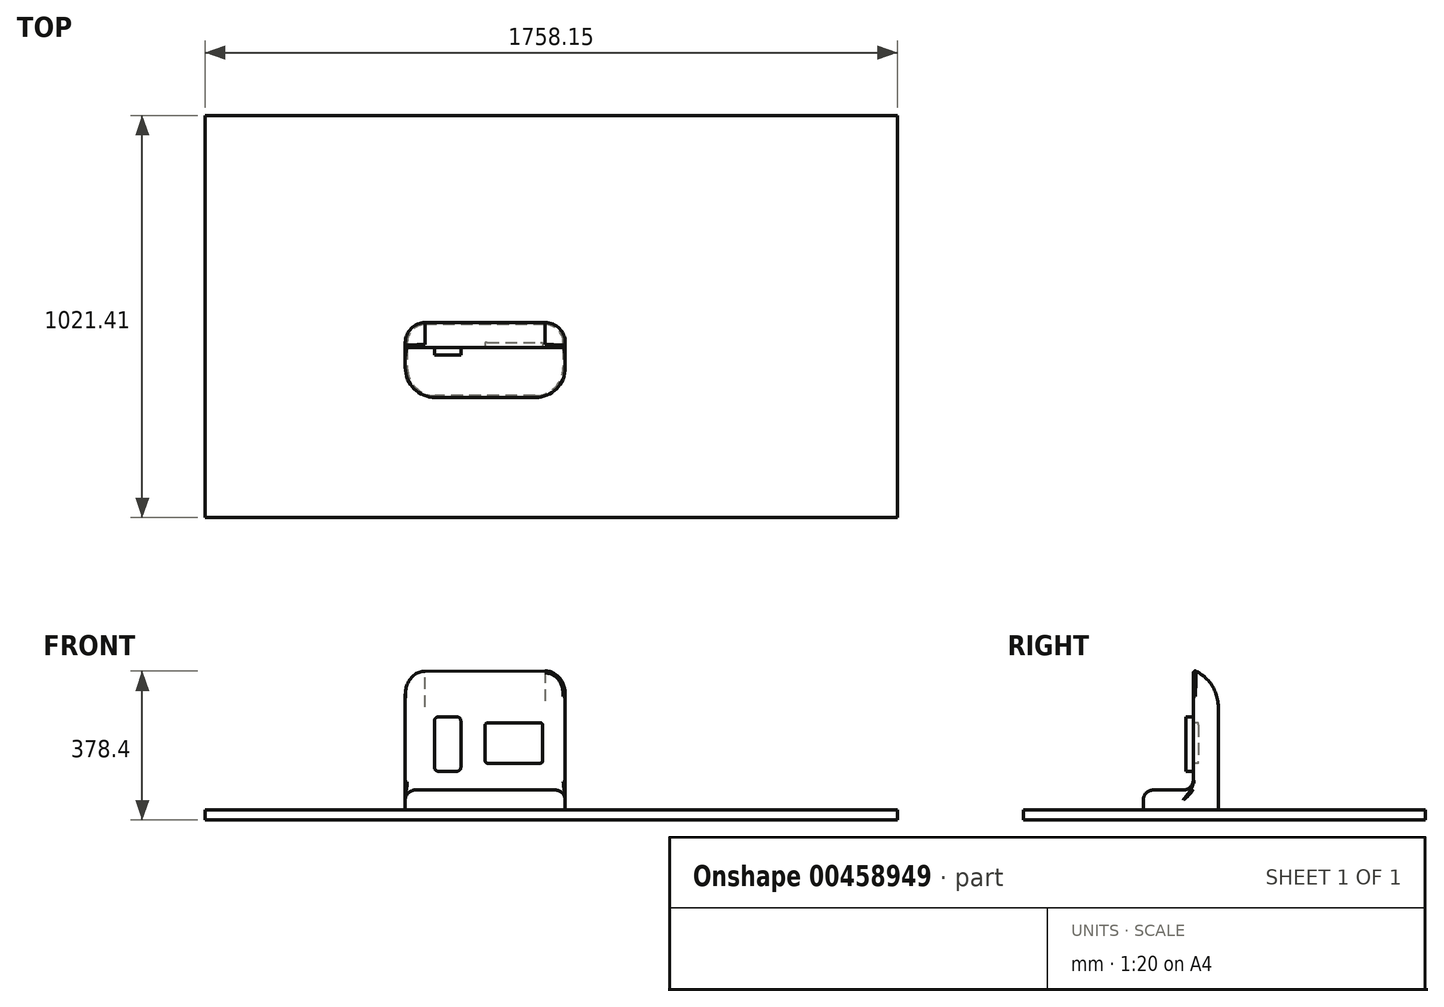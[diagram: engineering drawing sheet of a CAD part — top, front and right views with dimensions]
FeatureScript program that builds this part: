
annotation { "Feature Type Name" : "Feature", "Feature Type Description" : "" }
export const myFeature = defineFeature(function(context is Context, id is Id, definition is map)
    precondition{}
    {
        {
            var Q0;
            Q0=qCreatedBy(makeId("Front.planeOp"),FACE);
            var sketch = newSketch(context, id + "F0", { "sketchPlane" : qUnion([Q0])});
            skLineSegment(sketch, "E0", {"start": v(0, 0) * mm, "end": v(0, 355.6) * mm, "construction": true});
            skLineSegment(sketch, "E1", {"start": v(0, 355.6) * mm, "end": v(203.2, 355.35) * mm});
            skLineSegment(sketch, "E2.MirrorCS", {"start": v(0, 355.6) * mm, "end": v(-203.2, 355.35) * mm});
            skLineSegment(sketch, "E3", {"start": v(203.2, 355.35) * mm, "end": v(203.2, 0) * mm});
            skLineSegment(sketch, "E4", {"start": v(203.2, 0) * mm, "end": v(-203.2, 0.5) * mm});
            skLineSegment(sketch, "E5", {"start": v(-203.2, 0.5) * mm, "end": v(-203.2, 355.35) * mm});
            skSolve(sketch);
        }
        {
            var Q0;
            Q0=makeQuery(id+"F0.imprint","IMPRINT",FACE,{"disambiguationData":[TD([[makeQuery(id+"F0.imprint","IMPRINT",EDGE,{"derivedFrom":sQuery(id+"F0.wireOp",EDGE,"E1")}),-1.0]])]});
            extrude(context, id + "F1", {"entities" : qUnion([Q0]), "depth" : 63.5 * mm});
        }
        {
            var Q0;
            Q0=makeQuery(id+"F1.opExtrude","CAP_EDGE",EDGE,{"disambiguationData":[OSD([sQuery(id+"F0.wireOp",EDGE,"E2.MirrorCS")])],"isStart":true});
            fillet(context, id + "F2", {"entities" : qUnion([Q0]), "radius" : 101.6 * mm, "tangentPropagation" : true, "allowEdgeOverflow" : false});
        }
        {
            var Q0;
            Q0=makeQuery(id+"F1.opExtrude","CAP_EDGE",EDGE,{"disambiguationData":[OSD([sQuery(id+"F0.wireOp",EDGE,"E5")])],"isStart":true});
            var Q1;
            Q1=makeQuery(id+"F1.opExtrude","CAP_EDGE",EDGE,{"disambiguationData":[OSD([sQuery(id+"F0.wireOp",EDGE,"E3")])],"isStart":true});
            fillet(context, id + "F3", {"entities" : qUnion([Q0, Q1]), "radius" : 50.8 * mm, "tangentPropagation" : true, "allowEdgeOverflow" : false});
        }
        {
            var Q0;
            Q0=makeQuery(id+"F1.opExtrude","CAP_FACE",FACE,{"disambiguationData":[OSD([sQuery(id+"F0.wireOp",EDGE,"E1"),sQuery(id+"F0.wireOp",EDGE,"E2.MirrorCS"),sQuery(id+"F0.wireOp",EDGE,"E3"),sQuery(id+"F0.wireOp",EDGE,"E4"),sQuery(id+"F0.wireOp",EDGE,"E5")])],"isStart":false});
            var sketch = newSketch(context, id + "F4", { "sketchPlane" : qUnion([Q0])});
            skLineSegment(sketch, "E6.bottom", {"start": v(-129.19, 236.5) * mm, "end": v(-62.13, 236.5) * mm});
            skLineSegment(sketch, "E6.top", {"start": v(-129.19, 98.33) * mm, "end": v(-62.13, 98.33) * mm});
            skLineSegment(sketch, "E6.left", {"start": v(-129.19, 236.5) * mm, "end": v(-129.19, 98.33) * mm});
            skLineSegment(sketch, "E6.right", {"start": v(-62.13, 236.5) * mm, "end": v(-62.13, 98.33) * mm});
            skSolve(sketch);
        }
        {
            var Q0;
            Q0=makeQuery(id+"F4.imprint","IMPRINT",FACE,{"disambiguationData":[TD([[makeQuery(id+"F4.imprint","IMPRINT",EDGE,{"derivedFrom":sQuery(id+"F4.wireOp",EDGE,"E6.bottom")}),-1.0]])]});
            extrude(context, id + "F5", {"entities" : qUnion([Q0]), "operationType" : NewBodyOperationType.ADD, "depth" : 19.05 * mm});
        }
        {
            var Q0;
            Q0=makeQuery(id+"F5.opExtrude","SWEPT_EDGE",EDGE,{"disambiguationData":[OSD([sQuery(id+"F4.wireOp",EDGE,"E6.bottom"),sQuery(id+"F4.wireOp",EDGE,"E6.left")])]});
            var Q1;
            Q1=makeQuery(id+"F5.opExtrude","SWEPT_EDGE",EDGE,{"disambiguationData":[OSD([sQuery(id+"F4.wireOp",EDGE,"E6.bottom"),sQuery(id+"F4.wireOp",EDGE,"E6.right")])]});
            var Q2;
            Q2=makeQuery(id+"F5.opExtrude","SWEPT_EDGE",EDGE,{"disambiguationData":[OSD([sQuery(id+"F4.wireOp",EDGE,"E6.top"),sQuery(id+"F4.wireOp",EDGE,"E6.right")])]});
            var Q3;
            Q3=makeQuery(id+"F5.opExtrude","SWEPT_EDGE",EDGE,{"disambiguationData":[OSD([sQuery(id+"F4.wireOp",EDGE,"E6.top"),sQuery(id+"F4.wireOp",EDGE,"E6.left")])]});
            fillet(context, id + "F6", {"entities" : qUnion([Q0, Q1, Q2, Q3]), "radius" : 10.16 * mm, "tangentPropagation" : true, "allowEdgeOverflow" : false});
        }
        {
            var Q0;
            Q0=makeQuery(id+"F5.opExtrude","CAP_EDGE",EDGE,{"disambiguationData":[OSD([sQuery(id+"F4.wireOp",EDGE,"E6.right")])],"isStart":true});
            var Q1;
            Q1=makeQuery(id+"F6.opFillet","BLEND_EDGE",EDGE,{"blendedFrom":[makeQuery(id+"F5.opExtrude","SWEPT_EDGE",EDGE,{"disambiguationData":[OSD([sQuery(id+"F4.wireOp",EDGE,"E6.bottom"),sQuery(id+"F4.wireOp",EDGE,"E6.right")])]}),makeQuery(id+"F1.opExtrude","CAP_FACE",FACE,{"disambiguationData":[OSD([sQuery(id+"F0.wireOp",EDGE,"E1"),sQuery(id+"F0.wireOp",EDGE,"E2.MirrorCS"),sQuery(id+"F0.wireOp",EDGE,"E3"),sQuery(id+"F0.wireOp",EDGE,"E4"),sQuery(id+"F0.wireOp",EDGE,"E5")])],"isStart":false})],"blendedInto":[makeQuery(id+"F1.opExtrude","CAP_FACE",FACE,{"disambiguationData":[OSD([sQuery(id+"F0.wireOp",EDGE,"E1"),sQuery(id+"F0.wireOp",EDGE,"E2.MirrorCS"),sQuery(id+"F0.wireOp",EDGE,"E3"),sQuery(id+"F0.wireOp",EDGE,"E4"),sQuery(id+"F0.wireOp",EDGE,"E5")])],"isStart":false})]});
            var Q2;
            Q2=makeQuery(id+"F5.opExtrude","CAP_EDGE",EDGE,{"disambiguationData":[OSD([sQuery(id+"F4.wireOp",EDGE,"E6.bottom")])],"isStart":true});
            var Q3;
            Q3=makeQuery(id+"F6.opFillet","BLEND_EDGE",EDGE,{"blendedFrom":[makeQuery(id+"F5.opExtrude","SWEPT_EDGE",EDGE,{"disambiguationData":[OSD([sQuery(id+"F4.wireOp",EDGE,"E6.bottom"),sQuery(id+"F4.wireOp",EDGE,"E6.left")])]}),makeQuery(id+"F1.opExtrude","CAP_FACE",FACE,{"disambiguationData":[OSD([sQuery(id+"F0.wireOp",EDGE,"E1"),sQuery(id+"F0.wireOp",EDGE,"E2.MirrorCS"),sQuery(id+"F0.wireOp",EDGE,"E3"),sQuery(id+"F0.wireOp",EDGE,"E4"),sQuery(id+"F0.wireOp",EDGE,"E5")])],"isStart":false})],"blendedInto":[makeQuery(id+"F1.opExtrude","CAP_FACE",FACE,{"disambiguationData":[OSD([sQuery(id+"F0.wireOp",EDGE,"E1"),sQuery(id+"F0.wireOp",EDGE,"E2.MirrorCS"),sQuery(id+"F0.wireOp",EDGE,"E3"),sQuery(id+"F0.wireOp",EDGE,"E4"),sQuery(id+"F0.wireOp",EDGE,"E5")])],"isStart":false})]});
            var Q4;
            Q4=makeQuery(id+"F5.opExtrude","CAP_EDGE",EDGE,{"disambiguationData":[OSD([sQuery(id+"F4.wireOp",EDGE,"E6.left")])],"isStart":true});
            var Q5;
            Q5=makeQuery(id+"F6.opFillet","BLEND_EDGE",EDGE,{"blendedFrom":[makeQuery(id+"F5.opExtrude","SWEPT_EDGE",EDGE,{"disambiguationData":[OSD([sQuery(id+"F4.wireOp",EDGE,"E6.top"),sQuery(id+"F4.wireOp",EDGE,"E6.left")])]}),makeQuery(id+"F1.opExtrude","CAP_FACE",FACE,{"disambiguationData":[OSD([sQuery(id+"F0.wireOp",EDGE,"E1"),sQuery(id+"F0.wireOp",EDGE,"E2.MirrorCS"),sQuery(id+"F0.wireOp",EDGE,"E3"),sQuery(id+"F0.wireOp",EDGE,"E4"),sQuery(id+"F0.wireOp",EDGE,"E5")])],"isStart":false})],"blendedInto":[makeQuery(id+"F1.opExtrude","CAP_FACE",FACE,{"disambiguationData":[OSD([sQuery(id+"F0.wireOp",EDGE,"E1"),sQuery(id+"F0.wireOp",EDGE,"E2.MirrorCS"),sQuery(id+"F0.wireOp",EDGE,"E3"),sQuery(id+"F0.wireOp",EDGE,"E4"),sQuery(id+"F0.wireOp",EDGE,"E5")])],"isStart":false})]});
            var Q6;
            Q6=makeQuery(id+"F5.opExtrude","CAP_EDGE",EDGE,{"disambiguationData":[OSD([sQuery(id+"F4.wireOp",EDGE,"E6.top")])],"isStart":true});
            var Q7;
            Q7=makeQuery(id+"F6.opFillet","BLEND_EDGE",EDGE,{"blendedFrom":[makeQuery(id+"F5.opExtrude","SWEPT_EDGE",EDGE,{"disambiguationData":[OSD([sQuery(id+"F4.wireOp",EDGE,"E6.top"),sQuery(id+"F4.wireOp",EDGE,"E6.right")])]}),makeQuery(id+"F1.opExtrude","CAP_FACE",FACE,{"disambiguationData":[OSD([sQuery(id+"F0.wireOp",EDGE,"E1"),sQuery(id+"F0.wireOp",EDGE,"E2.MirrorCS"),sQuery(id+"F0.wireOp",EDGE,"E3"),sQuery(id+"F0.wireOp",EDGE,"E4"),sQuery(id+"F0.wireOp",EDGE,"E5")])],"isStart":false})],"blendedInto":[makeQuery(id+"F1.opExtrude","CAP_FACE",FACE,{"disambiguationData":[OSD([sQuery(id+"F0.wireOp",EDGE,"E1"),sQuery(id+"F0.wireOp",EDGE,"E2.MirrorCS"),sQuery(id+"F0.wireOp",EDGE,"E3"),sQuery(id+"F0.wireOp",EDGE,"E4"),sQuery(id+"F0.wireOp",EDGE,"E5")])],"isStart":false})]});
            fillet(context, id + "F7", {"entities" : qUnion([Q0, Q1, Q2, Q3, Q4, Q5, Q6, Q7]), "radius" : 5.08 * mm, "tangentPropagation" : true, "allowEdgeOverflow" : false});
        }
        {
            var Q0;
            Q0=qCreatedBy(makeId("Right.planeOp"),FACE);
            var sketch = newSketch(context, id + "F8", { "sketchPlane" : qUnion([Q0])});
            skLineSegment(sketch, "E7.bottom", {"start": v(0, 0) * mm, "end": v(-190.5, 0) * mm});
            skLineSegment(sketch, "E7.top", {"start": v(0, 50.8) * mm, "end": v(-190.5, 50.8) * mm});
            skLineSegment(sketch, "E7.left", {"start": v(0, 0) * mm, "end": v(0, 50.8) * mm});
            skLineSegment(sketch, "E7.right", {"start": v(-190.5, 0) * mm, "end": v(-190.5, 50.8) * mm});
            skSolve(sketch);
        }
        {
            var Q0;
            Q0=qSketchRegion(id+"F8",true);
            extrude(context, id + "F9", {"entities" : qUnion([Q0]), "operationType" : NewBodyOperationType.ADD, "depth" : 203.2 * mm, "hasSecondDirection" : true, "secondDirectionOppositeDirection" : true, "secondDirectionDepth" : 203.2 * mm});
        }
        {
            var Q0;
            Q0=makeQuery(id+"F9.opExtrude","CAP_EDGE",EDGE,{"disambiguationData":[OSD([sQuery(id+"F8.wireOp",EDGE,"E7.left")])],"isStart":true});
            fillet(context, id + "F10", {"entities" : qUnion([Q0]), "radius" : 50.8 * mm, "tangentPropagation" : true, "allowEdgeOverflow" : false});
        }
        {
            var Q0;
            Q0=makeQuery(id+"F9.opExtrude","CAP_EDGE",EDGE,{"disambiguationData":[OSD([sQuery(id+"F8.wireOp",EDGE,"E7.left")])],"isStart":false});
            fillet(context, id + "F11", {"entities" : qUnion([Q0]), "radius" : 50.8 * mm, "tangentPropagation" : true, "allowEdgeOverflow" : false});
        }
        {
            var Q0;
            Q0=makeQuery(id+"F9.opExtrude","CAP_EDGE",EDGE,{"disambiguationData":[OSD([sQuery(id+"F8.wireOp",EDGE,"E7.right")])],"isStart":true});
            var Q1;
            Q1=makeQuery(id+"F9.opExtrude","CAP_EDGE",EDGE,{"disambiguationData":[OSD([sQuery(id+"F8.wireOp",EDGE,"E7.right")])],"isStart":false});
            fillet(context, id + "F12", {"entities" : qUnion([Q0, Q1]), "radius" : 76.2 * mm, "tangentPropagation" : true, "allowEdgeOverflow" : false});
        }
        {
            var Q0;
            Q0=makeQuery(id+"F1.opExtrude","CAP_FACE",FACE,{"disambiguationData":[OSD([sQuery(id+"F0.wireOp",EDGE,"E1"),sQuery(id+"F0.wireOp",EDGE,"E2.MirrorCS"),sQuery(id+"F0.wireOp",EDGE,"E3"),sQuery(id+"F0.wireOp",EDGE,"E4"),sQuery(id+"F0.wireOp",EDGE,"E5")])],"isStart":false});
            var sketch = newSketch(context, id + "F13", { "sketchPlane" : qUnion([Q0])});
            skLineSegment(sketch, "E8.bottom", {"start": v(0, 221.12) * mm, "end": v(145.52, 221.12) * mm});
            skLineSegment(sketch, "E8.top", {"start": v(0, 118.96) * mm, "end": v(145.52, 118.96) * mm});
            skLineSegment(sketch, "E8.left", {"start": v(0, 221.12) * mm, "end": v(0, 118.96) * mm});
            skLineSegment(sketch, "E8.right", {"start": v(145.52, 221.12) * mm, "end": v(145.52, 118.96) * mm});
            skSolve(sketch);
        }
        {
            var Q0;
            Q0=makeQuery(id+"F9.opExtrude","SWEPT_EDGE",EDGE,{"disambiguationData":[OSD([sQuery(id+"F8.wireOp",EDGE,"E7.top"),sQuery(id+"F8.wireOp",EDGE,"E7.right")])]});
            fillet(context, id + "F14", {"entities" : qUnion([Q0]), "radius" : 25.4 * mm, "tangentPropagation" : true, "allowEdgeOverflow" : false});
        }
        {
            var Q0;
            Q0=makeQuery(id+"F9.boolean.opBoolean","INTERSECT",EDGE,{"derivedFrom":[makeQuery(id+"F1.opExtrude","CAP_FACE",FACE,{"disambiguationData":[OSD([sQuery(id+"F0.wireOp",EDGE,"E1"),sQuery(id+"F0.wireOp",EDGE,"E2.MirrorCS"),sQuery(id+"F0.wireOp",EDGE,"E3"),sQuery(id+"F0.wireOp",EDGE,"E4"),sQuery(id+"F0.wireOp",EDGE,"E5")])],"isStart":false}),makeQuery(id+"F9.opExtrude","SWEPT_FACE",FACE,{"disambiguationData":[OSD([sQuery(id+"F8.wireOp",EDGE,"E7.top")])]})]});
            fillet(context, id + "F15", {"entities" : qUnion([Q0]), "radius" : 25.4 * mm, "tangentPropagation" : true, "allowEdgeOverflow" : false});
        }
        {
            var Q0;
            {var subQ0=sQuery(id+"F8.wireOp",EDGE,"E7.right");var subQ1=sQuery(id+"F8.wireOp",EDGE,"E7.top");var subQ2=makeQuery(id+"F9.opExtrude","CAP_FACE",FACE,{"disambiguationData":[OSD([sQuery(id+"F8.wireOp",EDGE,"E7.bottom"),subQ1,sQuery(id+"F8.wireOp",EDGE,"E7.left"),subQ0])],"isStart":true});var subQ3=sQuery(id+"F0.wireOp",EDGE,"E5");var subQ4=makeQuery(id+"F1.opExtrude","CAP_FACE",FACE,{"disambiguationData":[OSD([sQuery(id+"F0.wireOp",EDGE,"E1"),sQuery(id+"F0.wireOp",EDGE,"E2.MirrorCS"),sQuery(id+"F0.wireOp",EDGE,"E3"),sQuery(id+"F0.wireOp",EDGE,"E4"),subQ3])],"isStart":false});Q0=makeQuery(id+"F15.opFillet","BLEND_EDGE",EDGE,{"blendedFrom":[makeQuery(id+"F14.opFillet","BLEND_EDGE",EDGE,{"blendedFrom":[makeQuery(id+"F9.boolean.opBoolean","SPLIT",EDGE,{"disambiguationData":[TD([makeQuery(id+"F9.opExtrude","SWEPT_FACE",FACE,{"disambiguationData":[OSD([subQ0])]})])],"derivedFrom":makeQuery(id+"F9.opExtrude","CAP_EDGE",EDGE,{"disambiguationData":[OSD([subQ1])],"isStart":true})}),subQ4],"blendedInto":[subQ4]}),subQ2],"blendedInto":[subQ2]});}
            var Q1;
            {var subQ0=sQuery(id+"F8.wireOp",EDGE,"E7.bottom");var subQ1=sQuery(id+"F8.wireOp",EDGE,"E7.top");var subQ3=sQuery(id+"F0.wireOp",EDGE,"E3");var subQ5=makeQuery(id+"F1.opExtrude","CAP_FACE",FACE,{"disambiguationData":[OSD([sQuery(id+"F0.wireOp",EDGE,"E1"),sQuery(id+"F0.wireOp",EDGE,"E2.MirrorCS"),subQ3,sQuery(id+"F0.wireOp",EDGE,"E4"),sQuery(id+"F0.wireOp",EDGE,"E5")])],"isStart":false});var subQ6=sQuery(id+"F8.wireOp",EDGE,"E7.right");var subQ7=makeQuery(id+"F9.opExtrude","SWEPT_FACE",FACE,{"disambiguationData":[OSD([subQ6])]});var subQ8=makeQuery(id+"F9.opExtrude","CAP_FACE",FACE,{"disambiguationData":[OSD([subQ0,subQ1,sQuery(id+"F8.wireOp",EDGE,"E7.left"),subQ6])],"isStart":false});Q1=makeQuery(id+"F15.opFillet","BLEND_EDGE",EDGE,{"blendedFrom":[makeQuery(id+"F14.opFillet","BLEND_EDGE",EDGE,{"blendedFrom":[makeQuery(id+"F9.boolean.opBoolean","SPLIT",EDGE,{"disambiguationData":[TD([subQ7])],"derivedFrom":makeQuery(id+"F9.opExtrude","CAP_EDGE",EDGE,{"disambiguationData":[OSD([subQ1])],"isStart":false})}),subQ5],"blendedInto":[subQ5]}),makeQuery(id+"F9.boolean.opBoolean","SPLIT",FACE,{"disambiguationData":[TD([subQ7])],"derivedFrom":subQ8})],"blendedInto":[makeQuery(id+"F9.boolean.opBoolean","SPLIT",FACE,{"disambiguationData":[TD([subQ7])],"derivedFrom":subQ8})]});}
            fillet(context, id + "F16", {"entities" : qUnion([Q0, Q1]), "radius" : 5.08 * mm, "tangentPropagation" : true, "allowEdgeOverflow" : false});
        }
        {
            var Q0;
            Q0=makeQuery(id+"F13.imprint","IMPRINT",FACE,{"disambiguationData":[TD([[makeQuery(id+"F13.imprint","IMPRINT",EDGE,{"derivedFrom":sQuery(id+"F13.wireOp",EDGE,"E8.bottom")}),-1.0]])]});
            extrude(context, id + "F17", {"entities" : qUnion([Q0]), "operationType" : NewBodyOperationType.REMOVE, "oppositeDirection" : true, "depth" : 12.7 * mm});
        }
        {
            var Q0;
            Q0=makeQuery(id+"F17.boolean.opBoolean","COPY",EDGE,{"derivedFrom":makeQuery(id+"F17.opExtrude","SWEPT_EDGE",EDGE,{"disambiguationData":[OSD([sQuery(id+"F13.wireOp",EDGE,"E8.bottom"),sQuery(id+"F13.wireOp",EDGE,"E8.left")])]})});
            var Q1;
            Q1=makeQuery(id+"F17.boolean.opBoolean","COPY",EDGE,{"derivedFrom":makeQuery(id+"F17.opExtrude","SWEPT_EDGE",EDGE,{"disambiguationData":[OSD([sQuery(id+"F13.wireOp",EDGE,"E8.bottom"),sQuery(id+"F13.wireOp",EDGE,"E8.right")])]})});
            var Q2;
            Q2=makeQuery(id+"F17.boolean.opBoolean","COPY",EDGE,{"derivedFrom":makeQuery(id+"F17.opExtrude","SWEPT_EDGE",EDGE,{"disambiguationData":[OSD([sQuery(id+"F13.wireOp",EDGE,"E8.top"),sQuery(id+"F13.wireOp",EDGE,"E8.left")])]})});
            var Q3;
            Q3=makeQuery(id+"F17.boolean.opBoolean","COPY",EDGE,{"derivedFrom":makeQuery(id+"F17.opExtrude","SWEPT_EDGE",EDGE,{"disambiguationData":[OSD([sQuery(id+"F13.wireOp",EDGE,"E8.top"),sQuery(id+"F13.wireOp",EDGE,"E8.right")])]})});
            fillet(context, id + "F18", {"entities" : qUnion([Q0, Q1, Q2, Q3]), "radius" : 5.08 * mm, "tangentPropagation" : true, "allowEdgeOverflow" : false});
        }
        {
            var Q0;
            Q0=makeQuery(id+"F9.opExtrude","SWEPT_EDGE",EDGE,{"disambiguationData":[OSD([sQuery(id+"F8.wireOp",EDGE,"E7.bottom"),sQuery(id+"F8.wireOp",EDGE,"E7.left")])]});
            fillet(context, id + "F19", {"entities" : qUnion([Q0]), "radius" : 5.08 * mm, "tangentPropagation" : true, "allowEdgeOverflow" : false});
        }
        {
            var Q0;
            Q0=makeQuery(id+"F9.opExtrude","SWEPT_FACE",FACE,{"disambiguationData":[OSD([sQuery(id+"F8.wireOp",EDGE,"E7.bottom")])]});
            var sketch = newSketch(context, id + "F20", { "sketchPlane" : qUnion([Q0])});
            skLineSegment(sketch, "E9.bottom", {"start": v(-711.22, 495.25) * mm, "end": v(1046.93, 495.25) * mm});
            skLineSegment(sketch, "E9.top", {"start": v(-711.22, -526.16) * mm, "end": v(1046.93, -526.16) * mm});
            skLineSegment(sketch, "E9.left", {"start": v(-711.22, 495.25) * mm, "end": v(-711.22, -526.16) * mm});
            skLineSegment(sketch, "E9.right", {"start": v(1046.93, 495.25) * mm, "end": v(1046.93, -526.16) * mm});
            skSolve(sketch);
        }
        {
            var Q0;
            Q0=qSketchRegion(id+"F20",true);
            extrude(context, id + "F21", {"entities" : qUnion([Q0]), "operationType" : NewBodyOperationType.ADD, "depth" : 25.4 * mm});
        }
    });
